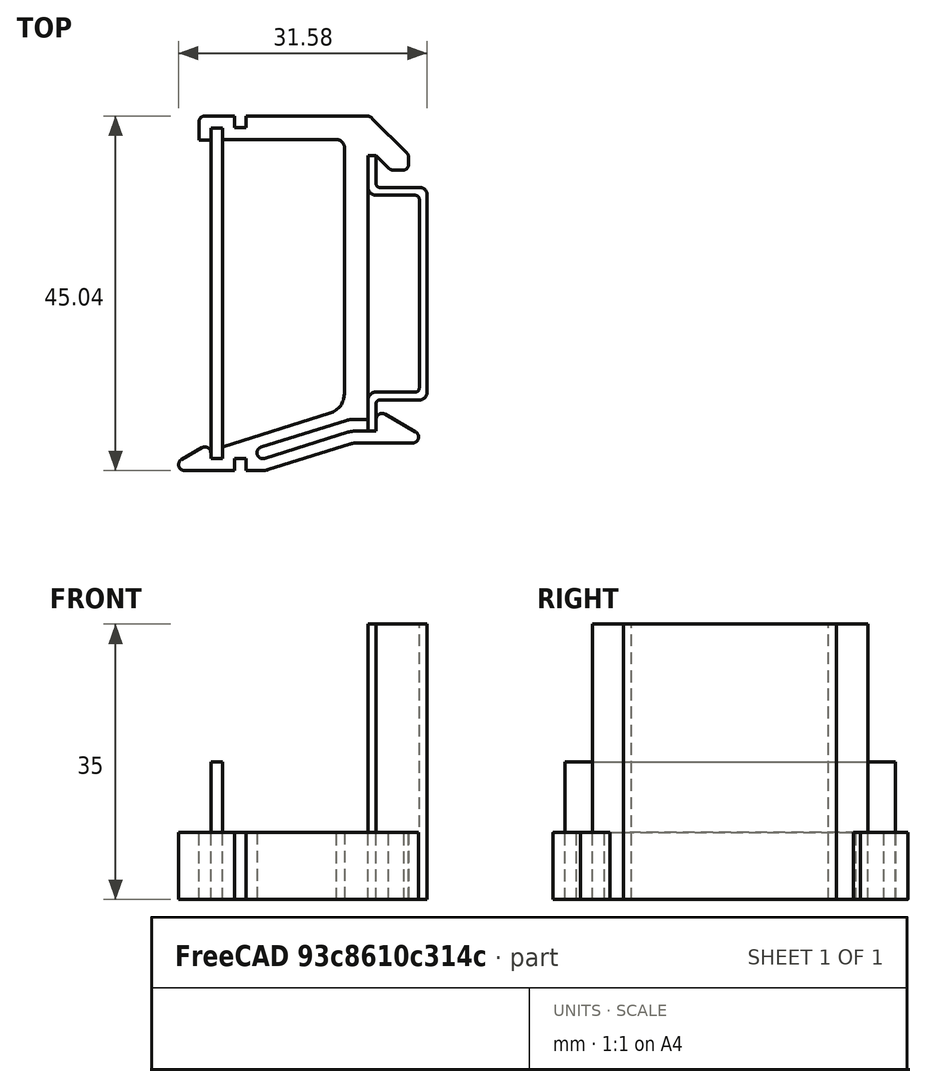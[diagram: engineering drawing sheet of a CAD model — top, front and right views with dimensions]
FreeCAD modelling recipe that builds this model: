
FCSTD DOCUMENT
Label: DIN_bracket_half
License: CC-BY 3.0
LicenseURL: http://creativecommons.org/licenses/by/3.0/
objects: Sketcher::SketchObject×2, PartDesign::Pad×2, Part::Box×1
note: 7 computed .brp shape members not serialized (recipe doc carries the construction recipe); baked Part::Feature solids carry a one-line shape summary decoded from their .brp

FEATURE [Sketcher::SketchObject] Sketch
  Placement = pos=(-3,0,0) rot=(0,0,1;0rad)
  sketch-geometry (52):
    g0: LineSegment StartX=2.77199 StartY=22.5417 StartZ=0 EndX=-12.5 EndY=22.5417 EndZ=0
    g1: LineSegment StartX=-18.5 StartY=21.7917 StartZ=0 EndX=-18.5 EndY=19.5 EndZ=0
    g2: LineSegment StartX=-18.5 StartY=19.5 StartZ=0 EndX=-17 EndY=19.5 EndZ=0
    g3: LineSegment StartX=-17 StartY=19.5 StartZ=0 EndX=-17 EndY=21 EndZ=0
    g4: LineSegment StartX=-17 StartY=21 StartZ=0 EndX=-15.5 EndY=21 EndZ=0
    g5: LineSegment StartX=-15.5 StartY=21 StartZ=0 EndX=-15.5 EndY=19.5417 EndZ=0
    g6: LineSegment StartX=-15.5 StartY=19.5417 StartZ=0 EndX=-1.04706 EndY=19.5417 EndZ=0
    g7: ArcOfCircle CenterX=-1.06574 CenterY=18.4761 CenterZ=0 NormalX=0 NormalY=0 NormalZ=1 Radius=1.06575 StartAngle=6.28199 EndAngle=7.83645
    g8: LineSegment StartX=0 StartY=18.4748 StartZ=0 EndX=-0.0372978 EndY=-12.7672 EndZ=0
    g9: LineSegment StartX=-15.5 StartY=-19.5 StartZ=0 EndX=-15.5 EndY=-21 EndZ=0
    g10: LineSegment StartX=-15.5 StartY=-21 StartZ=0 EndX=-17 EndY=-21 EndZ=0
    g11: LineSegment StartX=-17 StartY=-21 StartZ=0 EndX=-17 EndY=-20.25 EndZ=0
    g12: ArcOfCircle CenterX=-17.75 CenterY=-20.25 CenterZ=0 NormalX=0 NormalY=0 NormalZ=1 Radius=0.75 StartAngle=-3.81e-10 EndAngle=2.0944
    g13: LineSegment StartX=-18.125 StartY=-19.6005 StartZ=0 EndX=-20.7231 EndY=-21.1005 EndZ=0
    g14: ArcOfCircle CenterX=-20.3481 CenterY=-21.75 CenterZ=0 NormalX=0 NormalY=0 NormalZ=1 Radius=0.75 StartAngle=2.0944 EndAngle=4.71239
    g15: LineSegment StartX=-20.3481 StartY=-22.5 StartZ=0 EndX=-14 EndY=-22.5 EndZ=0
    g16: LineSegment StartX=1.57107 StartY=-19 StartZ=0 EndX=8.6469 EndY=-19 EndZ=0
    g17: ArcOfCircle CenterX=8.6469 CenterY=-18.25 CenterZ=0 NormalX=0 NormalY=0 NormalZ=1 Radius=0.75 StartAngle=4.71239 EndAngle=7.33038
    g18: LineSegment StartX=9.0219 StartY=-17.6005 StartZ=0 EndX=5.12479 EndY=-15.3505 EndZ=0
    g19: ArcOfCircle CenterX=4.74979 CenterY=-16 CenterZ=0 NormalX=0 NormalY=0 NormalZ=1 Radius=0.75 StartAngle=1.0472 EndAngle=3.14159
    g20: LineSegment StartX=3.99979 StartY=-17.5 StartZ=0 EndX=1.34107 EndY=-17.5 EndZ=0
    g21: LineSegment StartX=1.11107 StartY=-16 StartZ=0 EndX=2.99979 EndY=-16 EndZ=0
    g22: LineSegment StartX=2.99979 StartY=-16 StartZ=0 EndX=2.99979 EndY=17.5 EndZ=0
    g23: LineSegment StartX=2.99979 StartY=17.5 StartZ=0 EndX=3.99979 EndY=17.5 EndZ=0
    g24: LineSegment StartX=3.99979 StartY=17.5 StartZ=0 EndX=5.55694 EndY=15.9428 EndZ=0
    g25: ArcOfCircle CenterX=6.13336 CenterY=16.4227 CenterZ=0 NormalX=0 NormalY=0 NormalZ=1 Radius=0.75 StartAngle=3.83579 EndAngle=4.71239
    g26: LineSegment StartX=6.13336 StartY=15.6727 StartZ=0 EndX=7.5134 EndY=15.6727 EndZ=0
    g27: ArcOfCircle CenterX=7.37784 CenterY=16.4103 CenterZ=0 NormalX=0 NormalY=0 NormalZ=1 Radius=0.75 StartAngle=4.89412 EndAngle=6.45098
    g28: LineSegment StartX=8.11731 StartY=16.5356 StartZ=0 EndX=8.11731 EndY=17.3145 EndZ=0
    g29: LineSegment StartX=3.99979 StartY=-16 StartZ=0 EndX=3.99979 EndY=-17.5 EndZ=0
    g30: LineSegment StartX=-12.5 StartY=22.5417 StartZ=0 EndX=-12.5 EndY=21.0417 EndZ=0
    g31: LineSegment StartX=-12.5 StartY=21.0417 StartZ=0 EndX=-14 EndY=21.0417 EndZ=0
    g32: LineSegment StartX=-14 StartY=21.0417 StartZ=0 EndX=-14 EndY=22.5417 EndZ=0
    g33: LineSegment StartX=-14 StartY=22.5417 StartZ=0 EndX=-17.75 EndY=22.5417 EndZ=0
    g34: LineSegment StartX=3.50396 StartY=22.2385 StartZ=0 EndX=7.89764 EndY=17.8448 EndZ=0
    g35: ArcOfCircle CenterX=7.36731 CenterY=17.3145 CenterZ=0 NormalX=0 NormalY=0 NormalZ=1 Radius=0.75 StartAngle=0 EndAngle=0.785398
    g36: ArcOfCircle CenterX=2.77199 CenterY=21.5065 CenterZ=0 NormalX=0 NormalY=0 NormalZ=1 Radius=1.03517 StartAngle=0.785398 EndAngle=1.5708
    g37: ArcOfCircle CenterX=-17.75 CenterY=21.7917 CenterZ=0 NormalX=0 NormalY=0 NormalZ=1 Radius=0.75 StartAngle=1.5708 EndAngle=3.14159
    g38: LineSegment StartX=0.672204 StartY=-19.1378 StartZ=0 EndX=-9.70453 EndY=-22.3966 EndZ=0
    g39: LineSegment StartX=-15.5 StartY=-19.5 StartZ=0 EndX=-1.8307 EndY=-15.2072 EndZ=0
    g40: LineSegment StartX=0.212206 StartY=-16.1378 StartZ=0 EndX=-10.6034 EndY=-19.5345 EndZ=0
    g41: LineSegment StartX=-10.154 StartY=-20.9655 StartZ=0 EndX=0.442205 EndY=-17.6378 EndZ=0
    g42: ArcOfCircle CenterX=-10.3787 CenterY=-20.25 CenterZ=0 NormalX=0 NormalY=0 NormalZ=1 Radius=0.75 StartAngle=1.8751 EndAngle=5.01668
    g43: ArcOfCircle CenterX=-10.3787 CenterY=-20.25 CenterZ=0 NormalX=0 NormalY=0 NormalZ=1 Radius=2.25 StartAngle=4.71239 EndAngle=5.01668
    g44: LineSegment StartX=-14 StartY=-22.5 StartZ=0 EndX=-14 EndY=-21 EndZ=0
    g45: LineSegment StartX=-14 StartY=-21 StartZ=0 EndX=-12.5 EndY=-21 EndZ=0
    g46: LineSegment StartX=-12.5 StartY=-21 StartZ=0 EndX=-12.5 EndY=-22.5 EndZ=0
    g47: LineSegment StartX=-12.5 StartY=-22.5 StartZ=0 EndX=-10.3787 EndY=-22.5 EndZ=0
    g48: ArcOfCircle CenterX=-2.59792 CenterY=-12.7642 CenterZ=0 NormalX=0 NormalY=0 NormalZ=1 Radius=2.56062 StartAngle=5.01668 EndAngle=6.28199
    g49: ArcOfCircle CenterX=1.11107 CenterY=-19 CenterZ=0 NormalX=0 NormalY=0 NormalZ=1 Radius=3 StartAngle=1.5708 EndAngle=1.87509
    g50: ArcOfCircle CenterX=1.34107 CenterY=-20.5 CenterZ=0 NormalX=0 NormalY=0 NormalZ=1 Radius=3 StartAngle=1.5708 EndAngle=1.87509
    g51: ArcOfCircle CenterX=1.57107 CenterY=-22 CenterZ=0 NormalX=0 NormalY=0 NormalZ=1 Radius=3 StartAngle=1.5708 EndAngle=1.87509
  constraints (141):
    c: Vertical(g11)
    c: Distance(g10) = 1.5
    c: Coincident(g12,g11)
    c: Coincident(g11,g10)
    c: Coincident(g10,g9)
    c: Vertical(g9)
    c: Coincident(g14,g15)
    c: Horizontal(g15)
    c: Coincident(g13,g12)
    c: Tangent(g13,g12)
    c: Coincident(g21,g22)
    c: Vertical(g22)
    c: Parallel(g20,g21)
    c: Vertical(g29)
    c: Coincident(g19,g29)
    c: Coincident(g19,g18)
    c: Tangent(g19,g29)
    c: Tangent(g19,g18)
    c: Coincident(g29,g20)
    c: Coincident(g7,g8)
    c: Coincident(g23,g22)
    c: Coincident(g18,g17)
    c: Coincident(g7,g6)
    c: DistanceY(g21,g20) = -1.5
    c: Distance(g20,g16) = 1.5
    c: Coincident(g16,g17)
    c: DistanceX(g9) = -15.5
    c: DistanceX(g4) = -15.5
    c: Coincident(g5,g4)
    c: Vertical(g5)
    c: DistanceX(g4) = 1.5
    c: Vertical(g3)
    c: Coincident(g2,g3)
    c: Horizontal(g4)
    c: Vertical(g1)
    c: Coincident(g1,g2)
    c: DistanceX(g2) = 1.5
    c: DistanceY(g3) = 1.5
    c: Horizontal(g2)
    c: Tangent(g7,g8)
    c: DistanceX(g7) = 0
    c: Distance(g23) = 1
    c: Horizontal(g23)
    c: Coincident(g24,g23)
    c: Tangent(g25,g26)
    c: Horizontal(g0)
    c: Horizontal(g6)
    c: Coincident(g30,g31)
    c: Coincident(g31,g32)
    c: Horizontal(g31)
    c: Vertical(g30)
    c: Vertical(g32)
    c: Coincident(g0,g30)
    c: Coincident(g33,g32)
    c: Tangent(g0,g33)
    c: Distance(g31) = 1.5
    c: DistanceY(g32) = 1.5
    c: DistanceX(g31,g4) = -1.5
    c: Distance(g10,g15) = 1.5
    c: Parallel(g10,g15)
    c: Angle(g18,g16) = 0.523599
    c: Radius(g17) = 0.75
    c: DistanceX(g21,g20) = 1
    c: Distance(g29) = 1.5
    c: Radius(g19) = 0.75
    c: Tangent(g12,g11)
    c: Distance(g6,g0) = 3
    c: Vertical(g28)
    c: Coincident(g27,g28)
    c: Coincident(g26,g27)
    c: Horizontal(g26)
    c: Tangent(g17,g16)
    c: Coincident(g25,g24)
    c: Coincident(g25,g26)
    c: Tangent(g18,g17)
    c: Angle(g0,g34) = 2.35619
    c: Distance(g23,g34) = 3
    c: Parallel(g24,g34)
    c: Tangent(g28,g35)
    c: Tangent(g34,g35)
    c: Tangent(g0,g36)
    c: Tangent(g34,g36)
    c: Tangent(g1,g37)
    c: Tangent(g33,g37)
    c: Radius(g37) = 0.75
    c: Coincident(g4,g3)
    c: DistanceY(g3,g10) = -42
    c: DistanceY(g4) = 21
    c: Radius(g27) = 0.75
    c: Equal(g35,g27)
    c: Equal(g27,g25)
    c: Coincident(g5,g6)
    c: Distance(g9) = 1.5
    c: Parallel(g39,g38)
    c: Coincident(g9,g39)
    c: DistanceY(g20,g23) = 35
    c: Distance(g40,g39) = 1.5
    c: Distance(g41,g40) = 1.5
    c: Coincident(g42,g41)
    c: Tangent(g42,g41)
    c: Coincident(g42,g40)
    c: Tangent(g42,g40)
    c: Tangent(g47,g43)
    c: Tangent(g38,g43)
    c: Coincident(g43,g42)
    c: Parallel(g40,g41)
    c: Parallel(g20,g16)
    c: Horizontal(g16)
    c: DistanceY(g20) = -17.5
    c: Coincident(g14,g13)
    c: Tangent(g14,g13)
    c: Tangent(g14,g15)
    c: Angle(g15,g13) = 0.523599
    c: DistanceY(g11) = 0.75
    c: Radius(g12) = 0.75
    c: Radius(g14) = 0.75
    c: Coincident(g45,g46)
    c: DistanceX(g45) = 1.5
    c: Vertical(g46)
    c: Vertical(g44)
    c: Coincident(g44,g45)
    c: Coincident(g15,g44)
    c: Coincident(g47,g46)
    c: Tangent(g15,g47)
    c: DistanceY(g44) = 1.5
    c: Equal(g46,g44)
    c: DistanceX(g15,g9) = -1.5
    c: Distance(g38,g41) = 1.5
    c: Parallel(g39,g40)
    c: Tangent(g8,g48)
    c: Tangent(g39,g48)
    c: Distance(g42,g45) = 2.25
    c: Tangent(g21,g49)
    c: Tangent(g40,g49)
    c: Tangent(g20,g50)
    c: Tangent(g41,g50)
    c: Tangent(g16,g51)
    c: Tangent(g38,g51)
    c: Radius(g49) = 3
    c: Radius(g50) = 3
    c: Radius(g51) = 3
FEATURE [Sketcher::SketchObject] Sketch001
  Placement = pos=(0,17.5,0) rot=(0,0,1;0rad)
  sketch-geometry (20):
    g0: LineSegment StartX=0 StartY=0 StartZ=0 EndX=0.981065 EndY=0 EndZ=0
    g1: LineSegment StartX=0.981065 StartY=0 StartZ=0 EndX=0.981065 EndY=-3.53545 EndZ=0
    g2: ArcOfCircle CenterX=1.48107 CenterY=-3.53545 CenterZ=0 NormalX=0 NormalY=0 NormalZ=1 Radius=0.5 StartAngle=3.14159 EndAngle=4.71239
    g3: LineSegment StartX=1.48107 StartY=-4.03545 StartZ=0 EndX=6.48107 EndY=-4.03545 EndZ=0
    g4: ArcOfCircle CenterX=6.48107 CenterY=-5.03545 CenterZ=0 NormalX=0 NormalY=0 NormalZ=1 Radius=1 StartAngle=0 EndAngle=1.5708
    g5: LineSegment StartX=7.48107 StartY=-5.03545 StartZ=0 EndX=7.48107 EndY=-30.0354 EndZ=0
    g6: ArcOfCircle CenterX=6.48107 CenterY=-30.0354 CenterZ=0 NormalX=0 NormalY=0 NormalZ=1 Radius=1 StartAngle=4.71239 EndAngle=6.28319
    g7: LineSegment StartX=6.48107 StartY=-31.0354 StartZ=0 EndX=1.48107 EndY=-31.0354 EndZ=0
    g8: ArcOfCircle CenterX=1.48107 CenterY=-31.5354 CenterZ=0 NormalX=0 NormalY=0 NormalZ=1 Radius=0.5 StartAngle=1.5708 EndAngle=3.14159
    g9: LineSegment StartX=0.981065 StartY=-31.5354 StartZ=0 EndX=0.981065 EndY=-35 EndZ=0
    g10: LineSegment StartX=0.981065 StartY=-35 StartZ=0 EndX=-0.018935 EndY=-35 EndZ=0
    g11: LineSegment StartX=-0.018935 StartY=-35 StartZ=0 EndX=-0.018935 EndY=-31.0354 EndZ=0
    g12: ArcOfCircle CenterX=0.981065 CenterY=-31.0354 CenterZ=0 NormalX=0 NormalY=0 NormalZ=1 Radius=1 StartAngle=1.5708 EndAngle=3.14159
    g13: LineSegment StartX=0.981065 StartY=-30.0354 StartZ=0 EndX=5.98107 EndY=-30.0354 EndZ=0
    g14: ArcOfCircle CenterX=5.98107 CenterY=-29.5354 CenterZ=0 NormalX=0 NormalY=0 NormalZ=1 Radius=0.5 StartAngle=4.71239 EndAngle=6.28319
    g15: LineSegment StartX=6.48107 StartY=-29.5354 StartZ=0 EndX=6.48107 EndY=-5.53545 EndZ=0
    g16: ArcOfCircle CenterX=5.98107 CenterY=-5.53545 CenterZ=0 NormalX=0 NormalY=0 NormalZ=1 Radius=0.5 StartAngle=0 EndAngle=1.5708
    g17: LineSegment StartX=5.98107 StartY=-5.03545 StartZ=0 EndX=0.981065 EndY=-5.03545 EndZ=0
    g18: ArcOfCircle CenterX=0.981065 CenterY=-4.03545 CenterZ=0 NormalX=0 NormalY=0 NormalZ=1 Radius=1 StartAngle=3.14159 EndAngle=4.71239
    g19: LineSegment StartX=-0.018935 StartY=-4.03545 StartZ=0 EndX=0 EndY=0 EndZ=0
  constraints (9):
    c: DistanceY(g-1,g10) = -35
    c: DistanceX(g0) = 0
    c: DistanceY(g0) = 0
    c: Horizontal(g0)
    c: Coincident(g19,g-1)
    c: Coincident(g1,g0)
    c: Horizontal(g10)
    c: Coincident(g9,g10)
    c: Coincident(g11,g10)
FEATURE [PartDesign::Pad] Pad001  label="DIN rail"
  Length = 35
  Length2 = 100
  Placement = pos=(0,17.5,0) rot=(0,0,1;0rad)
  Sketch = -> Sketch001
  Type = 0
FEATURE [PartDesign::Pad] Pad  label="DIN bracket half"
  Length = 8.5
  Length2 = 100
  Placement = pos=(-3,0,0) rot=(0,0,1;0rad)
  Sketch = -> Sketch
  Type = 0
FEATURE [Part::Box] Box  label="PCB"
  Height = 17.5
  Length = 1.5
  Placement = pos=(-20,-21,0) rot=(0,0,1;0rad)
  Width = 42
